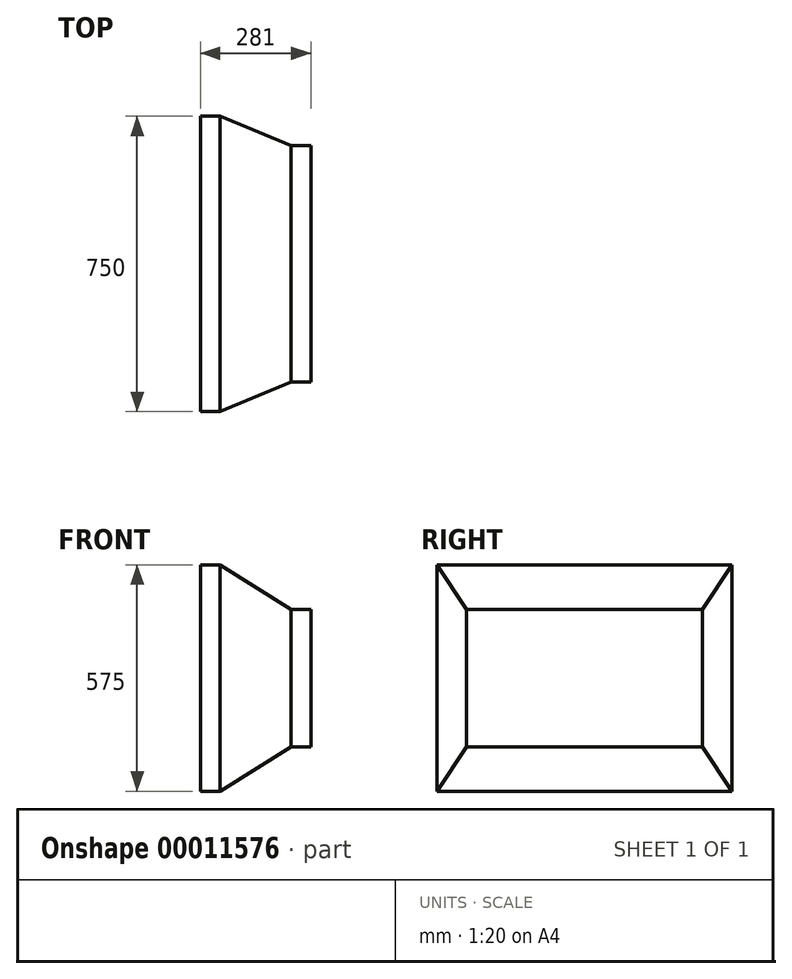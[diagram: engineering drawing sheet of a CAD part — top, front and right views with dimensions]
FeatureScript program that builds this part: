
annotation { "Feature Type Name" : "Feature", "Feature Type Description" : "" }
export const myFeature = defineFeature(function(context is Context, id is Id, definition is map)
    precondition{}
    {
        {
            var Q0;
            Q0=qCreatedBy(makeId("Right.planeOp"),FACE);
            var sketch = newSketch(context, id + "F0", { "sketchPlane" : qUnion([Q0])});
            skLineSegment(sketch, "E0.rect.bottom", {"start": v(-375, 287.5) * mm, "end": v(375, 287.5) * mm});
            skLineSegment(sketch, "E0.rect.top", {"start": v(-375, -287.5) * mm, "end": v(375, -287.5) * mm});
            skLineSegment(sketch, "E0.rect.left", {"start": v(-375, 287.5) * mm, "end": v(-375, -287.5) * mm});
            skLineSegment(sketch, "E0.rect.right", {"start": v(375, 287.5) * mm, "end": v(375, -287.5) * mm});
            skPoint(sketch, "E0.rect.middle", {"position": v(0, 0) * mm});
            skSolve(sketch);
        }
        {
            var Q0;
            Q0=makeQuery(id+"F0.imprint","IMPRINT",FACE,{"disambiguationData":[TD([[makeQuery(id+"F0.imprint","IMPRINT",EDGE,{"derivedFrom":sQuery(id+"F0.wireOp",EDGE,"E0.rect.bottom")}),-1.0]])]});
            extrude(context, id + "F1", {"entities" : qUnion([Q0]), "depth" : 50 * mm});
        }
        {
            var Q0;
            Q0=makeQuery(id+"F1.opExtrude","CAP_FACE",FACE,{"disambiguationData":[OSD([sQuery(id+"F0.wireOp",EDGE,"E0.rect.bottom"),sQuery(id+"F0.wireOp",EDGE,"E0.rect.top"),sQuery(id+"F0.wireOp",EDGE,"E0.rect.left"),sQuery(id+"F0.wireOp",EDGE,"E0.rect.right")])],"isStart":false});
            cPlane(context, id + "F2", {"entities" : qUnion([Q0]), "cplaneType" : CPlaneType.OFFSET, "offset" : 181 * mm, "width" : 150 * mm, "height" : 150 * mm});
        }
        {
            var Q0;
            Q0=qCreatedBy(id+"F2.planeOp",FACE);
            var sketch = newSketch(context, id + "F3", { "sketchPlane" : qUnion([Q0])});
            skLineSegment(sketch, "E1.rect.bottom", {"start": v(-300, 175) * mm, "end": v(300, 175) * mm});
            skLineSegment(sketch, "E1.rect.top", {"start": v(-300, -175) * mm, "end": v(300, -175) * mm});
            skLineSegment(sketch, "E1.rect.left", {"start": v(300, 175) * mm, "end": v(300, -175) * mm});
            skLineSegment(sketch, "E1.rect.right", {"start": v(-300, 175) * mm, "end": v(-300, -175) * mm});
            skPoint(sketch, "E1.rect.middle", {"position": v(0, 0) * mm});
            skSolve(sketch);
        }
        {
            var Q1;
            Q1=makeQuery(id+"F1.opExtrude","CAP_FACE",FACE,{"disambiguationData":[OSD([sQuery(id+"F0.wireOp",EDGE,"E0.rect.bottom"),sQuery(id+"F0.wireOp",EDGE,"E0.rect.top"),sQuery(id+"F0.wireOp",EDGE,"E0.rect.left"),sQuery(id+"F0.wireOp",EDGE,"E0.rect.right")])],"isStart":false});
            var Q2;
            Q2=makeQuery(id+"F3.imprint","IMPRINT",FACE,{"disambiguationData":[TD([[makeQuery(id+"F3.imprint","IMPRINT",EDGE,{"derivedFrom":sQuery(id+"F3.wireOp",EDGE,"E1.rect.bottom")}),-1.0]])]});
            loft(context, id + "F4", {"operationType" : NewBodyOperationType.ADD, "sheetProfilesArray" : [{ "sheetProfileEntities" : qUnion([Q1]) }, { "sheetProfileEntities" : qUnion([Q2]) }]});
        }
        {
            var Q0;
            Q0=makeQuery(id+"F4.opLoft","CAP_FACE",FACE,{"disambiguationData":[OSD([makeQuery(id+"F3.imprint","IMPRINT",FACE,{"disambiguationData":[TD([[makeQuery(id+"F3.imprint","IMPRINT",EDGE,{"derivedFrom":sQuery(id+"F3.wireOp",EDGE,"E1.rect.bottom")}),-1.0]])]})])],"isStart":true});
            extrude(context, id + "F5", {"entities" : qUnion([Q0]), "operationType" : NewBodyOperationType.ADD, "depth" : 50 * mm});
        }
    });
